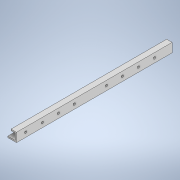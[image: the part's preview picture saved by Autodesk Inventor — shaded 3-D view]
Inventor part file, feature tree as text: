
AUTODESK INVENTOR PART (.ipt)
format: ipt  version: 2020 (Build 240168000, 168)  size: 126,464 bytes
history: native  units: in
note: dims shown in document units (in); Inventor stores cm internally (conversion verified against a paired STEP export)
features: extrude x1, sketch x1
ambient origin geometry x8: Origin, YZ Plane, XZ Plane, XY Plane, X Axis, Y Axis, Z Axis, Center Point
bodies: Solid2 (feature_tree), Solid1 (feature_tree)
feature tree (2):
  extrude  "Extrusion1"  Depth=0.12in
  sketch  "Sketch1"  dims[d0=2.5in d1=0.12in d2=0.75in d3=1.0in d4=0.0in]
